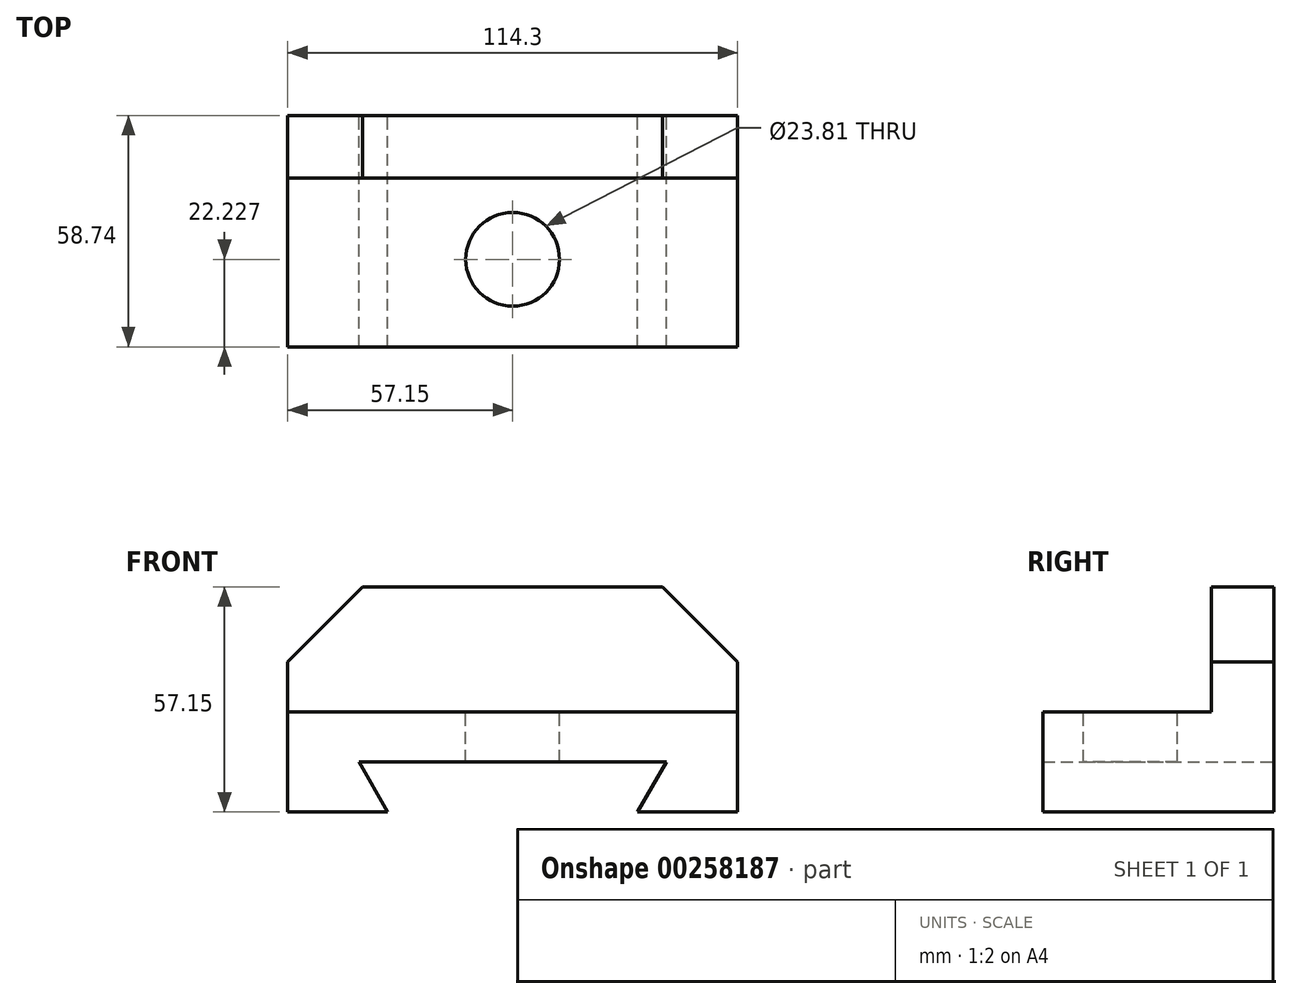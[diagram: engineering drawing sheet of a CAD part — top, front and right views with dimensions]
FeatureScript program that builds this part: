
annotation { "Feature Type Name" : "Feature", "Feature Type Description" : "" }
export const myFeature = defineFeature(function(context is Context, id is Id, definition is map)
    precondition{}
    {
        {
            var Q0;
            Q0=qCreatedBy(makeId("Front.planeOp"),FACE);
            var sketch = newSketch(context, id + "F0", { "sketchPlane" : qUnion([Q0])});
            skPoint(sketch, "E0.MirrorCS.end.orphan", {"position": v(31.75, 0) * mm});
            skPoint(sketch, "E0.MirrorCS.start.orphan", {"position": v(0, 0) * mm});
            skLineSegment(sketch, "E1", {"start": v(-31.75, -12.7) * mm, "end": v(-39.08, 0) * mm});
            skLineSegment(sketch, "E2", {"start": v(-57.15, -12.7) * mm, "end": v(-31.75, -12.7) * mm});
            skLineSegment(sketch, "E3", {"start": v(-39.08, 0) * mm, "end": v(0, 0) * mm});
            skLineSegment(sketch, "E4", {"start": v(-57.15, -12.7) * mm, "end": v(-57.15, 12.7) * mm});
            skLineSegment(sketch, "E5.MirrorCS", {"start": v(31.75, -12.7) * mm, "end": v(39.08, 0) * mm});
            skLineSegment(sketch, "E6.MirrorCS", {"start": v(57.15, -12.7) * mm, "end": v(57.15, 12.7) * mm});
            skLineSegment(sketch, "E7.MirrorCS", {"start": v(39.08, 0) * mm, "end": v(0, 0) * mm});
            skLineSegment(sketch, "E8.MirrorCS", {"start": v(57.15, -12.7) * mm, "end": v(31.75, -12.7) * mm});
            skLineSegment(sketch, "E9", {"start": v(-57.15, 12.7) * mm, "end": v(57.15, 12.7) * mm});
            skLineSegment(sketch, "E10", {"start": v(-38.1, 44.45) * mm, "end": v(0, 44.45) * mm});
            skLineSegment(sketch, "E11", {"start": v(-38.1, 44.45) * mm, "end": v(-55.63, 26.91) * mm});
            skLineSegment(sketch, "E12", {"start": v(-55.63, 26.91) * mm, "end": v(-57.15, 25.4) * mm});
            skLineSegment(sketch, "E13", {"start": v(-57.15, 25.4) * mm, "end": v(-57.15, 12.7) * mm});
            skPoint(sketch, "E14.orphan", {"position": v(-57.15, 44.45) * mm});
            skLineSegment(sketch, "E15.MirrorCS", {"start": v(55.63, 26.91) * mm, "end": v(57.15, 25.4) * mm});
            skPoint(sketch, "E16.MirrorP", {"position": v(57.15, 44.45) * mm});
            skLineSegment(sketch, "E17.MirrorCS", {"start": v(57.15, 25.4) * mm, "end": v(57.15, 12.7) * mm});
            skLineSegment(sketch, "E18.MirrorCS", {"start": v(38.1, 44.45) * mm, "end": v(55.63, 26.91) * mm});
            skLineSegment(sketch, "E19.MirrorCS", {"start": v(38.1, 44.45) * mm, "end": v(0, 44.45) * mm});
            skSolve(sketch);
        }
        {
            var Q0;
            Q0=makeQuery(id+"F0.imprint","IMPRINT",FACE,{"disambiguationData":[TD([[makeQuery(id+"F0.imprint","IMPRINT",EDGE,{"derivedFrom":sQuery(id+"F0.wireOp",EDGE,"E1")}),1.0]])]});
            extrude(context, id + "F1", {"entities" : qUnion([Q0]), "depth" : 58.74 * mm});
        }
        {
            var Q0;
            Q0=makeQuery(id+"F0.imprint","IMPRINT",FACE,{"disambiguationData":[TD([[makeQuery(id+"F0.imprint","IMPRINT",EDGE,{"derivedFrom":sQuery(id+"F0.wireOp",EDGE,"E9")}),1.0]])]});
            extrude(context, id + "F2", {"entities" : qUnion([Q0]), "operationType" : NewBodyOperationType.ADD, "depth" : 15.88 * mm});
        }
        {
            var Q0;
            Q0=makeQuery(id+"F1.opExtrude","SWEPT_FACE",FACE,{"disambiguationData":[OSD([sQuery(id+"F0.wireOp",EDGE,"E9")])]});
            var sketch = newSketch(context, id + "F3", { "sketchPlane" : qUnion([Q0])});
            skLineSegment(sketch, "E20", {"start": v(0, -58.74) * mm, "end": v(0, -36.51) * mm});
            skPoint(sketch, "E20.endSnap0", {"position": v(0, -58.74) * mm});
            skCircle(sketch, "E21", {"center": v(0, -36.51) * mm, "radius": 11.9 * mm});
            skSolve(sketch);
        }
        {
            var Q0;
            Q0 = qSketchRegion(id + "F3", true);
            extrude(context, id + "F4", {"entities" : qUnion([Q0]), "operationType" : NewBodyOperationType.REMOVE, "oppositeDirection" : true, "depth" : 12.7 * mm});
        }
    });
